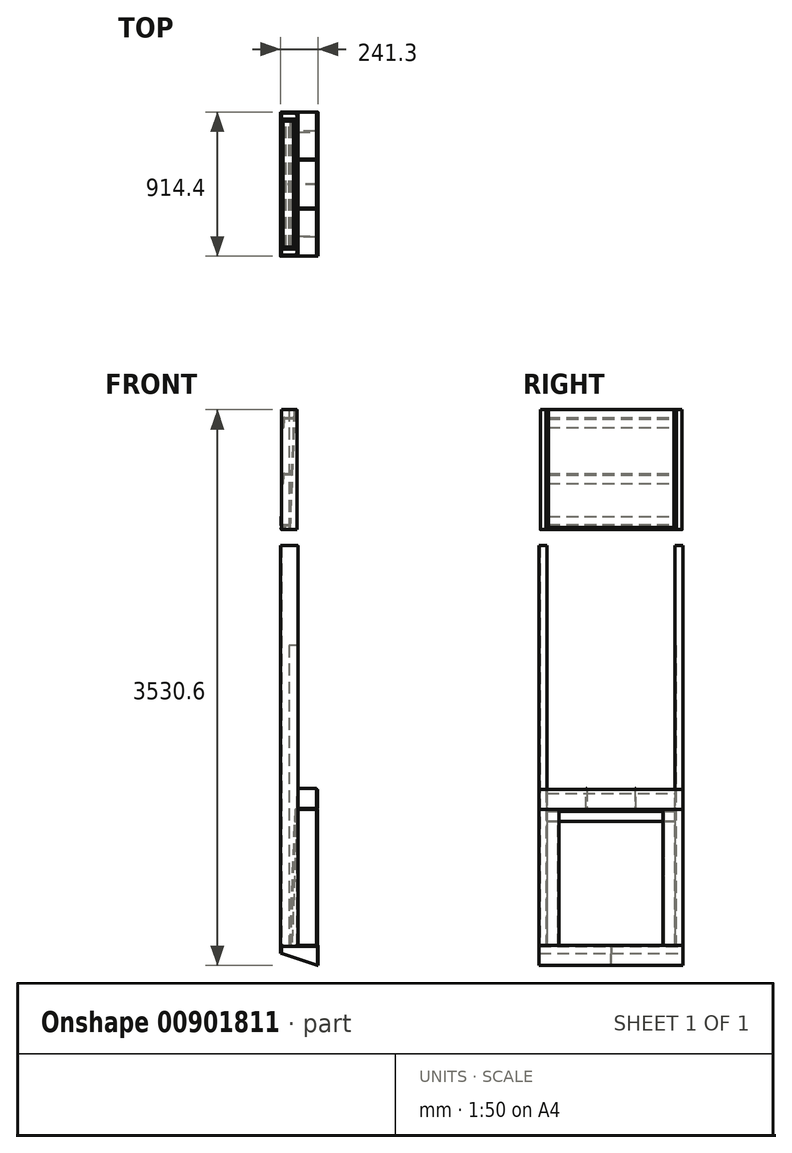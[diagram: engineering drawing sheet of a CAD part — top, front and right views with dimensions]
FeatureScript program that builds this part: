
annotation { "Feature Type Name" : "Feature", "Feature Type Description" : "" }
export const myFeature = defineFeature(function(context is Context, id is Id, definition is map)
    precondition{}
    {
        {
            var Q0;
            Q0=qCreatedBy(makeId("Front.planeOp"),FACE);
            var sketch = newSketch(context, id + "F0", { "sketchPlane" : qUnion([Q0])});
            skLineSegment(sketch, "E0", {"start": v(6.35, -50.8) * mm, "end": v(6.35, -19.05) * mm});
            skLineSegment(sketch, "E1", {"start": v(19.05, -6.35) * mm, "end": v(95.25, -6.35) * mm});
            skLineSegment(sketch, "E2", {"start": v(107.95, -19.05) * mm, "end": v(107.95, -127) * mm});
            skLineSegment(sketch, "E3", {"start": v(107.95, -127) * mm, "end": v(114.3, -127) * mm});
            skLineSegment(sketch, "E4", {"start": v(114.3, -127) * mm, "end": v(114.3, -12.7) * mm});
            skLineSegment(sketch, "E5", {"start": v(101.6, 0) * mm, "end": v(12.7, 0) * mm});
            skLineSegment(sketch, "E6", {"start": v(0, -12.7) * mm, "end": v(0, -50.8) * mm});
            skLineSegment(sketch, "E7", {"start": v(0, -50.8) * mm, "end": v(6.35, -50.8) * mm});
            skPoint(sketch, "E8.visualSharp", {"position": v(107.95, -6.35) * mm});
            skArc(sketch, "E8.filletArc", {"start": v(107.95, -19.05) * mm, "mid": v(104.23, -10.07) * mm, "end": v(95.25, -6.35) * mm});
            skPoint(sketch, "E9.visualSharp", {"position": v(6.35, -6.35) * mm});
            skArc(sketch, "E9.filletArc", {"start": v(19.05, -6.35) * mm, "mid": v(10.07, -10.07) * mm, "end": v(6.35, -19.05) * mm});
            skPoint(sketch, "E10.visualSharp", {"position": v(114.3, 0) * mm});
            skArc(sketch, "E10.filletArc", {"start": v(114.3, -12.7) * mm, "mid": v(110.58, -3.72) * mm, "end": v(101.6, 0) * mm});
            skPoint(sketch, "E11.visualSharp", {"position": v(0, 0) * mm});
            skArc(sketch, "E11.filletArc", {"start": v(12.7, 0) * mm, "mid": v(3.72, -3.72) * mm, "end": v(0, -12.7) * mm});
            skLineSegment(sketch, "E12", {"start": v(95.25, -6.35) * mm, "end": v(95.25, 0) * mm});
            skLineSegment(sketch, "E13", {"start": v(95.25, -6.35) * mm, "end": v(95.25, -127) * mm});
            skLineSegment(sketch, "E14", {"start": v(95.25, -127) * mm, "end": v(107.95, -127) * mm});
            skLineSegment(sketch, "E15", {"start": v(95.25, -6.35) * mm, "end": v(228.6, -6.35) * mm});
            skLineSegment(sketch, "E16", {"start": v(234.95, -12.7) * mm, "end": v(234.95, -127) * mm});
            skLineSegment(sketch, "E17", {"start": v(234.95, -127) * mm, "end": v(241.3, -127) * mm});
            skLineSegment(sketch, "E18", {"start": v(241.3, -127) * mm, "end": v(241.3, -6.35) * mm});
            skLineSegment(sketch, "E19", {"start": v(234.95, 0) * mm, "end": v(101.6, 0) * mm});
            skLineSegment(sketch, "E20", {"start": v(114.3, -12.7) * mm, "end": v(114.3, -6.35) * mm});
            skPoint(sketch, "E21.visualSharp", {"position": v(234.95, -6.35) * mm});
            skArc(sketch, "E21.filletArc", {"start": v(234.95, -12.7) * mm, "mid": v(233.1, -8.2) * mm, "end": v(228.6, -6.35) * mm});
            skPoint(sketch, "E22.visualSharp", {"position": v(241.3, 0) * mm});
            skArc(sketch, "E22.filletArc", {"start": v(241.3, -6.35) * mm, "mid": v(239.44, -1.86) * mm, "end": v(234.95, 0) * mm});
            skSolve(sketch);
        }
        {
            var Q0;
            Q0=makeQuery(id+"F0.imprint","IMPRINT",FACE,{"disambiguationData":[TD([[makeQuery(id+"F0.imprint","IMPRINT",EDGE,{"derivedFrom":sQuery(id+"F0.wireOp",EDGE,"E0")}),1.0]])]});
            var Q1;
            {var subQ3=sQuery(id+"F0.wireOp",EDGE,"E12");Q1=makeQuery(id+"F0.imprint","IMPRINT",FACE,{"disambiguationData":[TD([[makeQuery(id+"F0.imprint","IMPRINT",EDGE,{"derivedFrom":subQ3}),-1.0]])]});}
            extrude(context, id + "F1", {"entities" : qUnion([Q0, Q1]), "endBound" : BoundingType.SYMMETRIC, "depth" : 914.4 * mm, "offsetDistance" : 25.4 * mm});
        }
        {
            var Q0;
            Q0=makeQuery(id+"F1.opExtrude","SWEPT_FACE",FACE,{"disambiguationData":[OSD([sQuery(id+"F0.wireOp",EDGE,"E5")])]});
            var sketch = newSketch(context, id + "F2", { "sketchPlane" : qUnion([Q0])});
            skLineSegment(sketch, "E23", {"start": v(112.6, 406.4) * mm, "end": v(112.6, 444.5) * mm});
            skLineSegment(sketch, "E24", {"start": v(99.9, 457.2) * mm, "end": v(12.7, 457.2) * mm});
            skLineSegment(sketch, "E25", {"start": v(0, 444.5) * mm, "end": v(0, 406.4) * mm});
            skLineSegment(sketch, "E26", {"start": v(0, 406.4) * mm, "end": v(6.35, 406.4) * mm});
            skLineSegment(sketch, "E27", {"start": v(6.35, 406.4) * mm, "end": v(6.35, 438.15) * mm});
            skLineSegment(sketch, "E28", {"start": v(19.05, 450.85) * mm, "end": v(93.55, 450.85) * mm});
            skLineSegment(sketch, "E29", {"start": v(106.25, 438.15) * mm, "end": v(106.25, 406.4) * mm});
            skLineSegment(sketch, "E30", {"start": v(106.25, 406.4) * mm, "end": v(112.6, 406.4) * mm});
            skPoint(sketch, "E31.visualSharp", {"position": v(106.25, 450.85) * mm});
            skArc(sketch, "E31.filletArc", {"start": v(106.25, 438.15) * mm, "mid": v(102.53, 447.13) * mm, "end": v(93.55, 450.85) * mm});
            skPoint(sketch, "E32.visualSharp", {"position": v(112.6, 457.2) * mm});
            skArc(sketch, "E32.filletArc", {"start": v(112.6, 444.5) * mm, "mid": v(108.88, 453.48) * mm, "end": v(99.9, 457.2) * mm});
            skPoint(sketch, "E33.visualSharp", {"position": v(6.35, 450.85) * mm});
            skArc(sketch, "E33.filletArc", {"start": v(19.05, 450.85) * mm, "mid": v(10.07, 447.13) * mm, "end": v(6.35, 438.15) * mm});
            skPoint(sketch, "E34.visualSharp", {"position": v(0, 457.2) * mm});
            skArc(sketch, "E34.filletArc", {"start": v(12.7, 457.2) * mm, "mid": v(3.72, 453.48) * mm, "end": v(0, 444.5) * mm});
            skLineSegment(sketch, "E35", {"start": v(106.25, 406.4) * mm, "end": v(55.45, 406.4) * mm});
            skLineSegment(sketch, "E36", {"start": v(55.45, 406.4) * mm, "end": v(55.45, 412.75) * mm});
            skLineSegment(sketch, "E37", {"start": v(55.45, 412.75) * mm, "end": v(106.25, 412.75) * mm});
            skSolve(sketch);
        }
        {
            var Q0;
            Q0=makeQuery(id+"F2.imprint","IMPRINT",FACE,{"disambiguationData":[TD([[makeQuery(id+"F2.imprint","IMPRINT",EDGE,{"derivedFrom":sQuery(id+"F2.wireOp",EDGE,"E23")}),1.0]])]});
            var Q1;
            {var subQ5=sQuery(id+"F2.wireOp",EDGE,"E24");Q1=makeQuery(id+"F2.imprint","IMPRINT",FACE,{"disambiguationData":[TD([[makeQuery(id+"F2.imprint","IMPRINT",EDGE,{"derivedFrom":subQ5}),1.0]])]});}
            var Q2;
            Q2=makeQuery(id+"F2.imprint","IMPRINT",FACE,{"disambiguationData":[TD([[makeQuery(id+"F2.imprint","IMPRINT",EDGE,{"derivedFrom":sQuery(id+"F2.wireOp",EDGE,"E25")}),1.0]])]});
            extrude(context, id + "F3", {"entities" : qUnion([Q0, Q1, Q2]), "depth" : 2540 * mm, "offsetDistance" : 25.4 * mm});
        }
        {
            var Q0;
            Q0=makeQuery(id+"F3.opExtrude","SWEPT_BODY",BODY,{"disambiguationData":[OSD([sQuery(id+"F2.wireOp",EDGE,"E23"),sQuery(id+"F2.wireOp",EDGE,"E24"),sQuery(id+"F2.wireOp",EDGE,"E25"),sQuery(id+"F2.wireOp",EDGE,"E26"),sQuery(id+"F2.wireOp",EDGE,"E27"),sQuery(id+"F2.wireOp",EDGE,"E28"),sQuery(id+"F2.wireOp",EDGE,"E29"),sQuery(id+"F2.wireOp",EDGE,"E30"),sQuery(id+"F2.wireOp",EDGE,"E31.filletArc"),sQuery(id+"F2.wireOp",EDGE,"E32.filletArc"),sQuery(id+"F2.wireOp",EDGE,"E33.filletArc"),sQuery(id+"F2.wireOp",EDGE,"E34.filletArc")])]});
            var Q1;
            Q1=qCreatedBy(makeId("Front.planeOp"),FACE);
            mirror(context, id + "F4", {"operationType" : NewBodyOperationType.ADD, "entities" : qUnion([Q0]), "mirrorPlane" : qUnion([Q1])});
        }
        {
            var Q0;
            {var subQ1=sQuery(id+"F2.wireOp",EDGE,"E29");var subQ3=sQuery(id+"F2.wireOp",EDGE,"E37");var subQ4=makeQuery(id+"F2.imprint","INTERSECT",VERTEX,{"derivedFrom":[subQ1,subQ3]});Q0=makeQuery(id+"F2.imprint","IMPRINT",FACE,{"disambiguationData":[TD([[makeQuery(id+"F2.imprint","IMPRINT",EDGE,{"disambiguationData":[TD([[subQ4,-1.0]])],"derivedFrom":subQ1}),-1.0]])]});}
            var Q1;
            {var subQ0=sQuery(id+"F2.wireOp",EDGE,"E36");Q1=makeQuery(id+"F2.imprint","IMPRINT",FACE,{"disambiguationData":[TD([[makeQuery(id+"F2.imprint","IMPRINT",EDGE,{"derivedFrom":subQ0}),-1.0]])]});}
            extrude(context, id + "F5", {"entities" : qUnion([Q0, Q1]), "depth" : 1905 * mm, "offsetDistance" : 25.4 * mm});
        }
        {
            var Q0;
            Q0=makeQuery(id+"F5.opExtrude","SWEPT_BODY",BODY,{"disambiguationData":[OSD([sQuery(id+"F2.wireOp",EDGE,"E29"),sQuery(id+"F2.wireOp",EDGE,"E35"),sQuery(id+"F2.wireOp",EDGE,"E36"),sQuery(id+"F2.wireOp",EDGE,"E37")])]});
            var Q1;
            Q1=qCreatedBy(makeId("Front.planeOp"),FACE);
            mirror(context, id + "F6", {"entities" : qUnion([Q0]), "mirrorPlane" : qUnion([Q1])});
        }
        {
            var Q0;
            Q0=makeQuery(id+"F5.opExtrude","SWEPT_FACE",FACE,{"disambiguationData":[OSD([sQuery(id+"F2.wireOp",EDGE,"E35")])]});
            var sketch = newSketch(context, id + "F7", { "sketchPlane" : qUnion([Q0])});
            skLineSegment(sketch, "E38", {"start": v(68.15, 0) * mm, "end": v(99.9, 863.83) * mm});
            skLineSegment(sketch, "E39", {"start": v(99.9, 863.83) * mm, "end": v(106.25, 863.6) * mm});
            skLineSegment(sketch, "E40", {"start": v(106.25, 863.6) * mm, "end": v(74.5, 0) * mm});
            skLineSegment(sketch, "E41", {"start": v(74.5, 0) * mm, "end": v(68.15, 0) * mm});
            skLineSegment(sketch, "E42", {"start": v(106.25, 863.6) * mm, "end": v(112.6, 863.6) * mm});
            skLineSegment(sketch, "E43", {"start": v(112.6, 863.6) * mm, "end": v(112.6, 965.2) * mm});
            skLineSegment(sketch, "E44", {"start": v(112.6, 965.2) * mm, "end": v(106.25, 965.2) * mm});
            skLineSegment(sketch, "E45", {"start": v(106.25, 965.2) * mm, "end": v(106.25, 863.6) * mm});
            skLineSegment(sketch, "E46", {"start": v(106.25, 870.18) * mm, "end": v(99.9, 863.83) * mm});
            skLineSegment(sketch, "E47", {"start": v(112.6, 863.6) * mm, "end": v(105.82, 851.85) * mm});
            skLineSegment(sketch, "E48", {"start": v(103.45, 787.45) * mm, "end": v(97.1, 787.68) * mm});
            skSolve(sketch);
        }
        {
            var Q0;
            {var subQ4=sQuery(id+"F7.wireOp",EDGE,"E42");Q0=makeQuery(id+"F7.imprint","IMPRINT",FACE,{"disambiguationData":[TD([[makeQuery(id+"F7.imprint","IMPRINT",EDGE,{"derivedFrom":subQ4}),1.0]])]});}
            var Q1;
            {var subQ0=sQuery(id+"F7.wireOp",EDGE,"E39");Q1=makeQuery(id+"F7.imprint","IMPRINT",FACE,{"disambiguationData":[TD([[makeQuery(id+"F7.imprint","IMPRINT",EDGE,{"derivedFrom":subQ0}),1.0]])]});}
            var Q2;
            {var subQ0=sQuery(id+"F7.wireOp",EDGE,"E42");Q2=makeQuery(id+"F7.imprint","IMPRINT",FACE,{"disambiguationData":[TD([[makeQuery(id+"F7.imprint","IMPRINT",EDGE,{"derivedFrom":subQ0}),-1.0]])]});}
            var Q3;
            Q3=makeQuery(id+"F6.opPattern","COPY",FACE,{"derivedFrom":makeQuery(id+"F5.opExtrude","SWEPT_FACE",FACE,{"disambiguationData":[OSD([sQuery(id+"F2.wireOp",EDGE,"E35")])]}),"instanceName":"1"});
            extrude(context, id + "F8", {"entities" : qUnion([Q0, Q1, Q2]), "endBound" : BoundingType.UP_TO_SURFACE, "depth" : 25.4 * mm, "endBoundEntityFace" : qUnion([Q3]), "offsetDistance" : 25.4 * mm});
        }
        {
            var Q0;
            {var subQ3=sQuery(id+"F7.wireOp",EDGE,"E39");Q0=makeQuery(id+"F7.imprint","IMPRINT",FACE,{"disambiguationData":[TD([[makeQuery(id+"F7.imprint","IMPRINT",EDGE,{"derivedFrom":subQ3}),-1.0]])]});}
            var Q1;
            Q1=makeQuery(id+"F6.opPattern","COPY",FACE,{"derivedFrom":makeQuery(id+"F5.opExtrude","SWEPT_FACE",FACE,{"disambiguationData":[OSD([sQuery(id+"F2.wireOp",EDGE,"E35")])]}),"instanceName":"1"});
            extrude(context, id + "F9", {"entities" : qUnion([Q0]), "endBound" : BoundingType.UP_TO_SURFACE, "depth" : 25.4 * mm, "endBoundEntityFace" : qUnion([Q1]), "offsetDistance" : 25.4 * mm});
        }
        {
            var Q0;
            {var subQ0=sQuery(id+"F7.wireOp",EDGE,"E41");Q0=makeQuery(id+"F7.imprint","IMPRINT",FACE,{"disambiguationData":[TD([[makeQuery(id+"F7.imprint","IMPRINT",EDGE,{"derivedFrom":subQ0}),-1.0]])]});}
            extrude(context, id + "F10", {"entities" : qUnion([Q0]), "depth" : 76.2 * mm, "offsetDistance" : 25.4 * mm});
        }
        {
            var Q0;
            Q0=makeQuery(id+"F10.opExtrude","SWEPT_BODY",BODY,{"disambiguationData":[OSD([sQuery(id+"F7.wireOp",EDGE,"E38"),sQuery(id+"F7.wireOp",EDGE,"E40"),sQuery(id+"F7.wireOp",EDGE,"E41"),sQuery(id+"F7.wireOp",EDGE,"E48")])]});
            var Q1;
            Q1=qCreatedBy(makeId("Front.planeOp"),FACE);
            mirror(context, id + "F11", {"entities" : qUnion([Q0]), "mirrorPlane" : qUnion([Q1])});
        }
        {
            var Q0;
            Q0=makeQuery(id+"F1.opExtrude","SWEPT_FACE",FACE,{"disambiguationData":[OSD([sQuery(id+"F0.wireOp",EDGE,"E5")])]});
            var sketch = newSketch(context, id + "F12", { "sketchPlane" : qUnion([Q0])});
            skLineSegment(sketch, "E49", {"start": v(61.8, 406.4) * mm, "end": v(61.8, 330.2) * mm});
            skLineSegment(sketch, "E50", {"start": v(68.15, 330.2) * mm, "end": v(68.15, 406.4) * mm});
            skLineSegment(sketch, "E51", {"start": v(68.15, 406.4) * mm, "end": v(61.8, 406.4) * mm});
            skLineSegment(sketch, "E52", {"start": v(61.8, 330.2) * mm, "end": v(68.15, 330.2) * mm});
            skSolve(sketch);
        }
        {
            var Q0;
            Q0=makeQuery(id+"F12.imprint","IMPRINT",FACE,{"disambiguationData":[TD([[makeQuery(id+"F12.imprint","IMPRINT",EDGE,{"derivedFrom":sQuery(id+"F12.wireOp",EDGE,"E49")}),1.0]])]});
            var Q1;
            Q1=makeQuery(id+"F10.opExtrude","CAP_EDGE",EDGE,{"disambiguationData":[OSD([sQuery(id+"F7.wireOp",EDGE,"E38")])],"isStart":false});
            sweep(context, id + "F13", {"profiles" : qUnion([Q0]), "path" : qUnion([Q1])});
        }
        {
            var Q0;
            Q0=makeQuery(id+"F13.opSweep","SWEPT_BODY",BODY,{"disambiguationData":[OSD([sQuery(id+"F7.wireOp",EDGE,"E38"),sQuery(id+"F12.wireOp",EDGE,"E49"),sQuery(id+"F12.wireOp",EDGE,"E50"),sQuery(id+"F12.wireOp",EDGE,"E51"),sQuery(id+"F12.wireOp",EDGE,"E52")])]});
            var Q1;
            Q1=qCreatedBy(makeId("Front.planeOp"),FACE);
            mirror(context, id + "F14", {"entities" : qUnion([Q0]), "mirrorPlane" : qUnion([Q1])});
        }
        {
            var Q0;
            Q0=makeQuery(id+"F5.opExtrude","SWEPT_FACE",FACE,{"disambiguationData":[OSD([sQuery(id+"F2.wireOp",EDGE,"E35")])]});
            var sketch = newSketch(context, id + "F15", { "sketchPlane" : qUnion([Q0])});
            skLineSegment(sketch, "E53", {"start": v(90.75, 787.68) * mm, "end": v(93.56, 864.07) * mm});
            skLineSegment(sketch, "E54", {"start": v(97.1, 787.68) * mm, "end": v(99.9, 863.83) * mm});
            skLineSegment(sketch, "E55", {"start": v(93.56, 864.07) * mm, "end": v(99.9, 863.83) * mm});
            skLineSegment(sketch, "E56", {"start": v(97.1, 787.68) * mm, "end": v(90.75, 787.68) * mm});
            skSolve(sketch);
        }
        {
            var Q0;
            Q0=makeQuery(id+"F15.imprint","IMPRINT",FACE,{"disambiguationData":[TD([[makeQuery(id+"F15.imprint","IMPRINT",EDGE,{"derivedFrom":sQuery(id+"F15.wireOp",EDGE,"E53")}),-1.0]])]});
            var Q1;
            Q1=makeQuery(id+"F6.opPattern","COPY",FACE,{"derivedFrom":makeQuery(id+"F5.opExtrude","SWEPT_FACE",FACE,{"disambiguationData":[OSD([sQuery(id+"F2.wireOp",EDGE,"E35")])]}),"instanceName":"1"});
            extrude(context, id + "F16", {"entities" : qUnion([Q0]), "endBound" : BoundingType.UP_TO_SURFACE, "depth" : 25.4 * mm, "endBoundEntityFace" : qUnion([Q1]), "offsetDistance" : 25.4 * mm});
        }
        {
            var Q0;
            Q0=makeQuery(id+"F3.opExtrude","CAP_FACE",FACE,{"disambiguationData":[OSD([sQuery(id+"F2.wireOp",EDGE,"E23"),sQuery(id+"F2.wireOp",EDGE,"E24"),sQuery(id+"F2.wireOp",EDGE,"E25"),sQuery(id+"F2.wireOp",EDGE,"E26"),sQuery(id+"F2.wireOp",EDGE,"E27"),sQuery(id+"F2.wireOp",EDGE,"E28"),sQuery(id+"F2.wireOp",EDGE,"E29"),sQuery(id+"F2.wireOp",EDGE,"E30"),sQuery(id+"F2.wireOp",EDGE,"E31.filletArc"),sQuery(id+"F2.wireOp",EDGE,"E32.filletArc"),sQuery(id+"F2.wireOp",EDGE,"E33.filletArc"),sQuery(id+"F2.wireOp",EDGE,"E34.filletArc")])],"isStart":false});
            cPlane(context, id + "F17", {"entities" : qUnion([Q0]), "cplaneType" : CPlaneType.OFFSET, "offset" : 101.6 * mm, "width" : 152.4 * mm, "height" : 152.4 * mm});
        }
        {
            var Q0;
            Q0=qCreatedBy(id+"F17.planeOp",FACE);
            var sketch = newSketch(context, id + "F18", { "sketchPlane" : qUnion([Q0])});
            skLineSegment(sketch, "E57", {"start": v(104.98, 414.02) * mm, "end": v(7.62, 414.02) * mm});
            skLineSegment(sketch, "E58", {"start": v(7.62, 414.02) * mm, "end": v(7.62, 436.88) * mm});
            skLineSegment(sketch, "E59", {"start": v(20.32, 449.58) * mm, "end": v(92.28, 449.58) * mm});
            skLineSegment(sketch, "E60", {"start": v(104.98, 436.88) * mm, "end": v(104.98, 414.02) * mm});
            skPoint(sketch, "E61.visualSharp", {"position": v(104.98, 449.58) * mm});
            skArc(sketch, "E61.filletArc", {"start": v(104.98, 436.88) * mm, "mid": v(101.26, 445.86) * mm, "end": v(92.28, 449.58) * mm});
            skPoint(sketch, "E62.visualSharp", {"position": v(7.62, 449.58) * mm});
            skArc(sketch, "E62.filletArc", {"start": v(20.32, 449.58) * mm, "mid": v(11.34, 445.86) * mm, "end": v(7.62, 436.88) * mm});
            skLineSegment(sketch, "E63", {"start": v(54.18, 414.02) * mm, "end": v(54.18, 405.13) * mm});
            skLineSegment(sketch, "E64", {"start": v(54.18, 405.13) * mm, "end": v(7.62, 405.13) * mm});
            skLineSegment(sketch, "E65", {"start": v(7.62, 405.13) * mm, "end": v(7.62, 414.02) * mm});
            skLineSegment(sketch, "E66", {"start": v(54.18, 405.13) * mm, "end": v(61.8, 405.13) * mm});
            skLineSegment(sketch, "E67", {"start": v(61.8, 405.13) * mm, "end": v(61.8, 398.78) * mm});
            skLineSegment(sketch, "E68", {"start": v(61.8, 398.78) * mm, "end": v(7.62, 398.78) * mm});
            skLineSegment(sketch, "E69", {"start": v(7.62, 398.78) * mm, "end": v(7.62, 405.13) * mm});
            skSolve(sketch);
        }
        {
            var Q0;
            Q0=makeQuery(id+"F18.imprint","IMPRINT",FACE,{"disambiguationData":[TD([[makeQuery(id+"F18.imprint","IMPRINT",EDGE,{"derivedFrom":sQuery(id+"F18.wireOp",EDGE,"E57")}),-1.0]])]});
            extrude(context, id + "F19", {"entities" : qUnion([Q0]), "depth" : 762 * mm, "offsetDistance" : 25.4 * mm});
        }
        {
            var Q0;
            Q0=makeQuery(id+"F19.opExtrude","SWEPT_BODY",BODY,{"disambiguationData":[OSD([sQuery(id+"F18.wireOp",EDGE,"E57"),sQuery(id+"F18.wireOp",EDGE,"E58"),sQuery(id+"F18.wireOp",EDGE,"E59"),sQuery(id+"F18.wireOp",EDGE,"E60"),sQuery(id+"F18.wireOp",EDGE,"E61.filletArc"),sQuery(id+"F18.wireOp",EDGE,"E62.filletArc")])]});
            var Q1;
            Q1=qCreatedBy(makeId("Front.planeOp"),FACE);
            mirror(context, id + "F20", {"entities" : qUnion([Q0]), "mirrorPlane" : qUnion([Q1])});
        }
        {
            var Q0;
            {var subQ2=sQuery(id+"F18.wireOp",EDGE,"E63");Q0=makeQuery(id+"F18.imprint","IMPRINT",FACE,{"disambiguationData":[TD([[makeQuery(id+"F18.imprint","IMPRINT",EDGE,{"derivedFrom":subQ2}),-1.0]])]});}
            extrude(context, id + "F21", {"entities" : qUnion([Q0]), "depth" : 762 * mm, "offsetDistance" : 25.4 * mm});
        }
        {
            var Q0;
            Q0=makeQuery(id+"F21.opExtrude","CAP_FACE",FACE,{"disambiguationData":[OSD([sQuery(id+"F18.wireOp",EDGE,"E57"),sQuery(id+"F18.wireOp",EDGE,"E63"),sQuery(id+"F18.wireOp",EDGE,"E64"),sQuery(id+"F18.wireOp",EDGE,"E65")])],"isStart":false});
            var sketch = newSketch(context, id + "F22", { "sketchPlane" : qUnion([Q0])});
            skLineSegment(sketch, "E70", {"start": v(7.62, 405.13) * mm, "end": v(7.62, 398.78) * mm});
            skLineSegment(sketch, "E71", {"start": v(7.62, 398.78) * mm, "end": v(93.56, 398.78) * mm});
            skLineSegment(sketch, "E72", {"start": v(93.56, 398.78) * mm, "end": v(93.56, 405.13) * mm});
            skLineSegment(sketch, "E73", {"start": v(93.56, 405.13) * mm, "end": v(7.62, 405.13) * mm});
            skSolve(sketch);
        }
        {
            var Q1;
            {var subQ3=sQuery(id+"F22.wireOp",EDGE,"E70");Q1=makeQuery(id+"F22.imprint","IMPRINT",FACE,{"disambiguationData":[TD([[makeQuery(id+"F22.imprint","IMPRINT",EDGE,{"derivedFrom":subQ3}),1.0]])]});}
            var Q2;
            Q2=makeQuery(id+"F18.imprint","IMPRINT",FACE,{"disambiguationData":[TD([[makeQuery(id+"F18.imprint","IMPRINT",EDGE,{"derivedFrom":sQuery(id+"F18.wireOp",EDGE,"E64")}),1.0]])]});
            loft(context, id + "F23", {"sheetProfilesArray" : [{ "sheetProfileEntities" : qUnion([Q1]) }, { "sheetProfileEntities" : qUnion([Q2]) }]});
        }
        {
            var Q0;
            {var subQ3=sQuery(id+"F22.wireOp",EDGE,"E70");Q0=makeQuery(id+"F23.opLoft","SWEPT_BODY",BODY,{"disambiguationData":[OSD([makeQuery(id+"F18.imprint","IMPRINT",FACE,{"disambiguationData":[TD([[makeQuery(id+"F18.imprint","IMPRINT",EDGE,{"derivedFrom":sQuery(id+"F18.wireOp",EDGE,"E64")}),1.0]])]}),makeQuery(id+"F22.imprint","IMPRINT",FACE,{"disambiguationData":[TD([[makeQuery(id+"F22.imprint","IMPRINT",EDGE,{"derivedFrom":subQ3}),1.0]])]})])]});}
            var Q1;
            Q1=makeQuery(id+"F21.opExtrude","SWEPT_BODY",BODY,{"disambiguationData":[OSD([sQuery(id+"F18.wireOp",EDGE,"E57"),sQuery(id+"F18.wireOp",EDGE,"E63"),sQuery(id+"F18.wireOp",EDGE,"E64"),sQuery(id+"F18.wireOp",EDGE,"E65")])]});
            var Q2;
            Q2=qCreatedBy(makeId("Front.planeOp"),FACE);
            mirror(context, id + "F24", {"entities" : qUnion([Q0, Q1]), "mirrorPlane" : qUnion([Q2])});
        }
        {
            var Q0;
            Q0=makeQuery(id+"F23.opLoft","SWEPT_FACE",FACE,{"disambiguationData":[OSD([sQuery(id+"F18.wireOp",EDGE,"E67"),sQuery(id+"F18.wireOp",EDGE,"E68"),sQuery(id+"F18.wireOp",EDGE,"E69"),sQuery(id+"F22.wireOp",EDGE,"E70"),sQuery(id+"F22.wireOp",EDGE,"E71"),sQuery(id+"F22.wireOp",EDGE,"E72")])]});
            var sketch = newSketch(context, id + "F25", { "sketchPlane" : qUnion([Q0])});
            skLineSegment(sketch, "E74", {"start": v(93.56, 3403.6) * mm, "end": v(87.22, 3403.86) * mm});
            skLineSegment(sketch, "E75", {"start": v(87.22, 3403.86) * mm, "end": v(55.98, 2654.55) * mm});
            skLineSegment(sketch, "E76", {"start": v(55.98, 2654.55) * mm, "end": v(62.33, 2654.29) * mm});
            skLineSegment(sketch, "E77", {"start": v(62.33, 2654.29) * mm, "end": v(93.56, 3403.6) * mm});
            skLineSegment(sketch, "E78", {"start": v(5.97, 2667) * mm, "end": v(5.97, 2673.35) * mm});
            skLineSegment(sketch, "E79", {"start": v(5.97, 2673.35) * mm, "end": v(56.77, 2673.35) * mm});
            skLineSegment(sketch, "E80", {"start": v(5.97, 2667) * mm, "end": v(56.5, 2667) * mm});
            skLineSegment(sketch, "E81", {"start": v(56.5, 2667) * mm, "end": v(56.77, 2673.35) * mm});
            skLineSegment(sketch, "E82", {"start": v(36.38, 2641.6) * mm, "end": v(36.38, 2650.5) * mm});
            skLineSegment(sketch, "E83", {"start": v(36.38, 2650.5) * mm, "end": v(5.97, 2650.5) * mm});
            skLineSegment(sketch, "E84", {"start": v(5.97, 2650.5) * mm, "end": v(5.97, 2667) * mm});
            skLineSegment(sketch, "E85", {"start": v(5.97, 2650.5) * mm, "end": v(5.97, 2641.6) * mm});
            skLineSegment(sketch, "E86", {"start": v(5.97, 2641.6) * mm, "end": v(36.38, 2641.6) * mm});
            skLineSegment(sketch, "E87", {"start": v(5.97, 2644.14) * mm, "end": v(36.38, 2644.14) * mm});
            skLineSegment(sketch, "E88", {"start": v(5.97, 2673.35) * mm, "end": v(5.97, 2724.15) * mm});
            skLineSegment(sketch, "E89", {"start": v(5.97, 2724.15) * mm, "end": v(12.32, 2724.15) * mm});
            skLineSegment(sketch, "E90", {"start": v(12.32, 2724.15) * mm, "end": v(12.32, 2673.35) * mm});
            skSolve(sketch);
        }
        {
            var Q0;
            {var subQ0=sQuery(id+"F25.wireOp",EDGE,"E76");Q0=makeQuery(id+"F25.imprint","IMPRINT",FACE,{"disambiguationData":[TD([[makeQuery(id+"F25.imprint","IMPRINT",EDGE,{"derivedFrom":subQ0}),1.0]])]});}
            var Q1;
            Q1=makeQuery(id+"F24.opPattern","COPY",FACE,{"derivedFrom":makeQuery(id+"F23.opLoft","SWEPT_FACE",FACE,{"disambiguationData":[OSD([sQuery(id+"F18.wireOp",EDGE,"E67"),sQuery(id+"F18.wireOp",EDGE,"E68"),sQuery(id+"F18.wireOp",EDGE,"E69"),sQuery(id+"F22.wireOp",EDGE,"E70"),sQuery(id+"F22.wireOp",EDGE,"E71"),sQuery(id+"F22.wireOp",EDGE,"E72")])]}),"instanceName":"1"});
            extrude(context, id + "F26", {"entities" : qUnion([Q0]), "endBound" : BoundingType.UP_TO_SURFACE, "depth" : 25.4 * mm, "endBoundEntityFace" : qUnion([Q1]), "offsetDistance" : 25.4 * mm});
        }
        {
            var Q0;
            {var subQ0=sQuery(id+"F25.wireOp",EDGE,"E87");var subQ1=sQuery(id+"F25.wireOp",EDGE,"E82");var subQ2=makeQuery(id+"F25.imprint","INTERSECT",VERTEX,{"derivedFrom":[subQ1,subQ0]});var subQ9=sQuery(id+"F25.wireOp",EDGE,"E85");var subQ11=makeQuery(id+"F25.imprint","INTERSECT",VERTEX,{"derivedFrom":[subQ9,subQ0]});Q0=qUnion([makeQuery(id+"F25.imprint","IMPRINT",FACE,{"disambiguationData":[TD([[makeQuery(id+"F25.imprint","IMPRINT",EDGE,{"disambiguationData":[TD([[subQ11,1.0]])],"derivedFrom":subQ9}),1.0]])]}),makeQuery(id+"F25.imprint","IMPRINT",FACE,{"disambiguationData":[TD([[makeQuery(id+"F25.imprint","IMPRINT",EDGE,{"disambiguationData":[TD([[subQ2,-1.0]])],"derivedFrom":subQ1}),1.0]])]})]);}
            var Q1;
            Q1=makeQuery(id+"F24.opPattern","COPY",FACE,{"derivedFrom":makeQuery(id+"F23.opLoft","SWEPT_FACE",FACE,{"disambiguationData":[OSD([sQuery(id+"F18.wireOp",EDGE,"E67"),sQuery(id+"F18.wireOp",EDGE,"E68"),sQuery(id+"F18.wireOp",EDGE,"E69"),sQuery(id+"F22.wireOp",EDGE,"E70"),sQuery(id+"F22.wireOp",EDGE,"E71"),sQuery(id+"F22.wireOp",EDGE,"E72")])]}),"instanceName":"1"});
            extrude(context, id + "F27", {"entities" : qUnion([Q0]), "endBound" : BoundingType.UP_TO_SURFACE, "depth" : 25.4 * mm, "endBoundEntityFace" : qUnion([Q1]), "offsetDistance" : 25.4 * mm});
        }
        {
            var Q0;
            {var subQ8=sQuery(id+"F25.wireOp",EDGE,"E76");Q0=makeQuery(id+"F25.imprint","IMPRINT",FACE,{"disambiguationData":[TD([[makeQuery(id+"F25.imprint","IMPRINT",EDGE,{"derivedFrom":subQ8}),-1.0]])]});}
            var Q1;
            Q1=makeQuery(id+"F24.opPattern","COPY",FACE,{"derivedFrom":makeQuery(id+"F23.opLoft","SWEPT_FACE",FACE,{"disambiguationData":[OSD([sQuery(id+"F18.wireOp",EDGE,"E67"),sQuery(id+"F18.wireOp",EDGE,"E68"),sQuery(id+"F18.wireOp",EDGE,"E69"),sQuery(id+"F22.wireOp",EDGE,"E70"),sQuery(id+"F22.wireOp",EDGE,"E71"),sQuery(id+"F22.wireOp",EDGE,"E72")])]}),"instanceName":"1"});
            extrude(context, id + "F28", {"entities" : qUnion([Q0]), "endBound" : BoundingType.UP_TO_SURFACE, "depth" : 25.4 * mm, "endBoundEntityFace" : qUnion([Q1]), "offsetDistance" : 25.4 * mm});
        }
        {
            var Q0;
            {var subQ0=sQuery(id+"F25.wireOp",EDGE,"E78");Q0=makeQuery(id+"F25.imprint","IMPRINT",FACE,{"disambiguationData":[TD([[makeQuery(id+"F25.imprint","IMPRINT",EDGE,{"derivedFrom":subQ0}),-1.0]])]});}
            var Q1;
            {var subQ0=sQuery(id+"F25.wireOp",EDGE,"E80");var subQ1=sQuery(id+"F25.wireOp",EDGE,"E75");var subQ2=makeQuery(id+"F25.imprint","INTERSECT",VERTEX,{"derivedFrom":[subQ1,subQ0]});Q1=makeQuery(id+"F25.imprint","IMPRINT",FACE,{"disambiguationData":[TD([[makeQuery(id+"F25.imprint","IMPRINT",EDGE,{"disambiguationData":[TD([[subQ2,1.0]])],"derivedFrom":subQ1}),-1.0]])]});}
            var Q2;
            {var subQ0=sQuery(id+"F25.wireOp",EDGE,"E90");Q2=makeQuery(id+"F25.imprint","IMPRINT",FACE,{"disambiguationData":[TD([[makeQuery(id+"F25.imprint","IMPRINT",EDGE,{"derivedFrom":subQ0}),-1.0]])]});}
            var Q3;
            {var subQ0=sQuery(id+"F25.wireOp",EDGE,"E88");Q3=makeQuery(id+"F25.imprint","IMPRINT",FACE,{"disambiguationData":[TD([[makeQuery(id+"F25.imprint","IMPRINT",EDGE,{"derivedFrom":subQ0}),-1.0]])]});}
            var Q4;
            Q4=makeQuery(id+"F24.opPattern","COPY",FACE,{"derivedFrom":makeQuery(id+"F23.opLoft","SWEPT_FACE",FACE,{"disambiguationData":[OSD([sQuery(id+"F18.wireOp",EDGE,"E67"),sQuery(id+"F18.wireOp",EDGE,"E68"),sQuery(id+"F18.wireOp",EDGE,"E69"),sQuery(id+"F22.wireOp",EDGE,"E70"),sQuery(id+"F22.wireOp",EDGE,"E71"),sQuery(id+"F22.wireOp",EDGE,"E72")])]}),"instanceName":"1"});
            extrude(context, id + "F29", {"entities" : qUnion([Q0, Q1, Q2, Q3]), "endBound" : BoundingType.UP_TO_SURFACE, "depth" : 25.4 * mm, "endBoundEntityFace" : qUnion([Q4]), "offsetDistance" : 25.4 * mm});
        }
        {
            var Q0;
            {var subQ0=sQuery(id+"F0.wireOp",EDGE,"E16");Q0=makeQuery(id+"F0.imprint","IMPRINT",FACE,{"disambiguationData":[TD([[makeQuery(id+"F0.imprint","IMPRINT",EDGE,{"derivedFrom":subQ0}),1.0]])]});}
            extrude(context, id + "F30", {"entities" : qUnion([Q0]), "operationType" : NewBodyOperationType.ADD, "endBound" : BoundingType.SYMMETRIC, "depth" : 914.4 * mm, "offsetDistance" : 25.4 * mm});
        }
        {
            var Q0;
            Q0=makeQuery(id+"F23.opLoft","SWEPT_FACE",FACE,{"disambiguationData":[OSD([sQuery(id+"F18.wireOp",EDGE,"E67"),sQuery(id+"F18.wireOp",EDGE,"E68"),sQuery(id+"F18.wireOp",EDGE,"E69"),sQuery(id+"F22.wireOp",EDGE,"E70"),sQuery(id+"F22.wireOp",EDGE,"E71"),sQuery(id+"F22.wireOp",EDGE,"E72")])]});
            var sketch = newSketch(context, id + "F31", { "sketchPlane" : qUnion([Q0])});
            skLineSegment(sketch, "E91", {"start": v(21.27, 3346.46) * mm, "end": v(18.89, 3289.36) * mm});
            skLineSegment(sketch, "E92", {"start": v(18.89, 3289.36) * mm, "end": v(25.23, 3289.1) * mm});
            skLineSegment(sketch, "E93", {"start": v(25.23, 3289.1) * mm, "end": v(27.35, 3339.85) * mm});
            skLineSegment(sketch, "E94", {"start": v(33.96, 3345.93) * mm, "end": v(84.71, 3343.81) * mm});
            skLineSegment(sketch, "E95", {"start": v(84.71, 3343.81) * mm, "end": v(84.98, 3350.16) * mm});
            skLineSegment(sketch, "E96", {"start": v(84.98, 3350.16) * mm, "end": v(27.88, 3352.54) * mm});
            skLineSegment(sketch, "E97", {"start": v(-22.3, 24.23) * mm, "end": v(-24.94, -39.21) * mm});
            skLineSegment(sketch, "E98", {"start": v(-24.94, -39.21) * mm, "end": v(-18.6, -39.48) * mm});
            skLineSegment(sketch, "E99", {"start": v(-18.6, -39.48) * mm, "end": v(-16.21, 17.62) * mm});
            skLineSegment(sketch, "E100", {"start": v(-16.21, 17.62) * mm, "end": v(40.89, 15.24) * mm});
            skLineSegment(sketch, "E101", {"start": v(40.89, 15.24) * mm, "end": v(41.15, 21.59) * mm});
            skLineSegment(sketch, "E102", {"start": v(41.15, 21.59) * mm, "end": v(-22.3, 24.23) * mm});
            skPoint(sketch, "E103.visualSharp", {"position": v(27.61, 3346.2) * mm});
            skArc(sketch, "E103.filletArc", {"start": v(33.96, 3345.93) * mm, "mid": v(29.4, 3344.26) * mm, "end": v(27.35, 3339.85) * mm});
            skPoint(sketch, "E104.visualSharp", {"position": v(21.53, 3352.8) * mm});
            skArc(sketch, "E104.filletArc", {"start": v(27.88, 3352.54) * mm, "mid": v(23.31, 3350.86) * mm, "end": v(21.27, 3346.46) * mm});
            skSolve(sketch);
        }
        {
            var Q0;
            Q0=makeQuery(id+"F31.imprint","IMPRINT",FACE,{"disambiguationData":[TD([[makeQuery(id+"F31.imprint","IMPRINT",EDGE,{"derivedFrom":sQuery(id+"F31.wireOp",EDGE,"E91")}),-1.0]])]});
            var sketch = newSketch(context, id + "F32", { "sketchPlane" : qUnion([Q0])});
            skLineSegment(sketch, "E105", {"start": v(19.17, 2990.86) * mm, "end": v(15.62, 2933.82) * mm});
            skLineSegment(sketch, "E106", {"start": v(15.62, 2933.82) * mm, "end": v(21.96, 2933.43) * mm});
            skLineSegment(sketch, "E107", {"start": v(21.96, 2933.43) * mm, "end": v(25.11, 2984.13) * mm});
            skLineSegment(sketch, "E108", {"start": v(31.84, 2990.07) * mm, "end": v(69.87, 2987.71) * mm});
            skLineSegment(sketch, "E109", {"start": v(69.87, 2987.71) * mm, "end": v(70.26, 2994.05) * mm});
            skLineSegment(sketch, "E110", {"start": v(70.26, 2994.05) * mm, "end": v(25.9, 2996.8) * mm});
            skPoint(sketch, "E111.visualSharp", {"position": v(25.5, 2990.47) * mm});
            skArc(sketch, "E111.filletArc", {"start": v(31.84, 2990.07) * mm, "mid": v(27.25, 2988.5) * mm, "end": v(25.11, 2984.13) * mm});
            skPoint(sketch, "E112.visualSharp", {"position": v(19.56, 2997.2) * mm});
            skArc(sketch, "E112.filletArc", {"start": v(25.9, 2996.8) * mm, "mid": v(21.3, 2995.23) * mm, "end": v(19.17, 2990.86) * mm});
            skSolve(sketch);
        }
        {
            var Q0;
            Q0=makeQuery(id+"F31.imprint","IMPRINT",FACE,{"disambiguationData":[TD([[makeQuery(id+"F31.imprint","IMPRINT",EDGE,{"derivedFrom":sQuery(id+"F31.wireOp",EDGE,"E91")}),1.0]])]});
            var Q1;
            {var subQ1=sQuery(id+"F32.wireOp",EDGE,"E107");Q1=makeQuery(id+"F32.imprint","IMPRINT",FACE,{"disambiguationData":[TD([[makeQuery(id+"F32.imprint","IMPRINT",EDGE,{"derivedFrom":subQ1}),1.0]])]});}
            var Q2;
            {var subQ0=sQuery(id+"F32.wireOp",EDGE,"E105");Q2=makeQuery(id+"F32.imprint","IMPRINT",FACE,{"disambiguationData":[TD([[makeQuery(id+"F32.imprint","IMPRINT",EDGE,{"derivedFrom":subQ0}),1.0]])]});}
            var Q3;
            Q3=makeQuery(id+"F24.opPattern","COPY",FACE,{"derivedFrom":makeQuery(id+"F23.opLoft","SWEPT_FACE",FACE,{"disambiguationData":[OSD([sQuery(id+"F18.wireOp",EDGE,"E67"),sQuery(id+"F18.wireOp",EDGE,"E68"),sQuery(id+"F18.wireOp",EDGE,"E69"),sQuery(id+"F22.wireOp",EDGE,"E70"),sQuery(id+"F22.wireOp",EDGE,"E71"),sQuery(id+"F22.wireOp",EDGE,"E72")])]}),"instanceName":"1"});
            extrude(context, id + "F33", {"entities" : qUnion([Q0, Q1, Q2]), "endBound" : BoundingType.UP_TO_SURFACE, "depth" : 25.4 * mm, "endBoundEntityFace" : qUnion([Q3]), "offsetDistance" : 25.4 * mm});
        }
        {
            var Q0;
            {var subQ7=sQuery(id+"F2.wireOp",EDGE,"E24");var subQ10=sQuery(id+"F0.wireOp",EDGE,"E11.filletArc");var subQ13=sQuery(id+"F0.wireOp",EDGE,"E5");var subQ14=makeQuery(id+"F1.opExtrude","SWEPT_FACE",FACE,{"disambiguationData":[OSD([subQ13])]});var subQ15=makeQuery(id+"F3.opExtrude","SWEPT_FACE",FACE,{"disambiguationData":[OSD([subQ7])]});Q0=makeQuery(id+"F30.boolean.opBoolean","MERGE",FACE,{"derivedFrom":[makeQuery(id+"F4.boolean.opBoolean","SPLIT",FACE,{"disambiguationData":[TD([subQ15])],"derivedFrom":subQ14}),makeQuery(id+"F4.boolean.opBoolean","SPLIT",FACE,{"disambiguationData":[TD([makeQuery(id+"F4.opPattern","COPY",FACE,{"derivedFrom":subQ15,"instanceName":"1"})])],"derivedFrom":subQ14}),makeQuery(id+"F4.boolean.opBoolean","SPLIT",FACE,{"disambiguationData":[TD([makeQuery(id+"F1.opExtrude","SWEPT_FACE",FACE,{"disambiguationData":[OSD([subQ10])]})])],"derivedFrom":subQ14}),makeQuery(id+"F30.opExtrude","SWEPT_FACE",FACE,{"disambiguationData":[OSD([sQuery(id+"F0.wireOp",EDGE,"E19")])]})]});}
            var sketch = newSketch(context, id + "F34", { "sketchPlane" : qUnion([Q0])});
            skLineSegment(sketch, "E113", {"start": v(228.6, -457.2) * mm, "end": v(228.6, -342.9) * mm});
            skLineSegment(sketch, "E114", {"start": v(222.25, -336.55) * mm, "end": v(118.95, -336.55) * mm});
            skLineSegment(sketch, "E115", {"start": v(112.6, -342.9) * mm, "end": v(112.6, -406.4) * mm});
            skLineSegment(sketch, "E116", {"start": v(112.6, -406.4) * mm, "end": v(106.25, -406.4) * mm});
            skLineSegment(sketch, "E117", {"start": v(106.25, -406.4) * mm, "end": v(106.25, -336.55) * mm});
            skLineSegment(sketch, "E118", {"start": v(112.6, -330.2) * mm, "end": v(228.6, -330.2) * mm});
            skLineSegment(sketch, "E119", {"start": v(234.95, -336.55) * mm, "end": v(234.95, -457.2) * mm});
            skLineSegment(sketch, "E120", {"start": v(234.95, -457.2) * mm, "end": v(228.6, -457.2) * mm});
            skPoint(sketch, "E121.visualSharp", {"position": v(228.6, -336.55) * mm});
            skArc(sketch, "E121.filletArc", {"start": v(228.6, -342.9) * mm, "mid": v(226.74, -338.4) * mm, "end": v(222.25, -336.55) * mm});
            skPoint(sketch, "E122.visualSharp", {"position": v(112.6, -336.55) * mm});
            skArc(sketch, "E122.filletArc", {"start": v(118.95, -336.55) * mm, "mid": v(114.46, -338.4) * mm, "end": v(112.6, -342.9) * mm});
            skPoint(sketch, "E123.visualSharp", {"position": v(106.25, -330.2) * mm});
            skArc(sketch, "E123.filletArc", {"start": v(112.6, -330.2) * mm, "mid": v(108.1, -332.06) * mm, "end": v(106.25, -336.55) * mm});
            skPoint(sketch, "E124.visualSharp", {"position": v(234.95, -330.2) * mm});
            skArc(sketch, "E124.filletArc", {"start": v(234.95, -336.55) * mm, "mid": v(233.1, -332.06) * mm, "end": v(228.6, -330.2) * mm});
            skSolve(sketch);
        }
        {
            var Q0;
            Q0=makeQuery(id+"F34.imprint","IMPRINT",FACE,{"disambiguationData":[TD([[makeQuery(id+"F34.imprint","IMPRINT",EDGE,{"derivedFrom":sQuery(id+"F34.wireOp",EDGE,"E113")}),-1.0]])]});
            var Q1;
            Q1=makeQuery(id+"F8.opExtrude","SWEPT_FACE",FACE,{"disambiguationData":[OSD([sQuery(id+"F7.wireOp",EDGE,"E44")])]});
            extrude(context, id + "F35", {"entities" : qUnion([Q0]), "depth" : 863.6 * mm, "endBoundEntityFace" : qUnion([Q1]), "offsetDistance" : 25.4 * mm});
        }
        {
            var Q0;
            Q0=makeQuery(id+"F35.opExtrude","SWEPT_BODY",BODY,{"disambiguationData":[OSD([sQuery(id+"F34.wireOp",EDGE,"E113"),sQuery(id+"F34.wireOp",EDGE,"E114"),sQuery(id+"F34.wireOp",EDGE,"E115"),sQuery(id+"F34.wireOp",EDGE,"E116"),sQuery(id+"F34.wireOp",EDGE,"E117"),sQuery(id+"F34.wireOp",EDGE,"E118"),sQuery(id+"F34.wireOp",EDGE,"E119"),sQuery(id+"F34.wireOp",EDGE,"E120"),sQuery(id+"F34.wireOp",EDGE,"E121.filletArc"),sQuery(id+"F34.wireOp",EDGE,"E122.filletArc"),sQuery(id+"F34.wireOp",EDGE,"E123.filletArc"),sQuery(id+"F34.wireOp",EDGE,"E124.filletArc")])]});
            var Q1;
            Q1=qCreatedBy(makeId("Front.planeOp"),FACE);
            mirror(context, id + "F36", {"entities" : qUnion([Q0]), "mirrorPlane" : qUnion([Q1])});
        }
        {
            var Q0;
            Q0=makeQuery(id+"F11.opPattern","COPY",FACE,{"derivedFrom":makeQuery(id+"F10.opExtrude","SWEPT_FACE",FACE,{"disambiguationData":[OSD([sQuery(id+"F7.wireOp",EDGE,"E40")])]}),"instanceName":"1"});
            var sketch = newSketch(context, id + "F37", { "sketchPlane" : qUnion([Q0])});
            skLineSegment(sketch, "E125", {"start": v(-330.2, 790.72) * mm, "end": v(-336.55, 787.72) * mm});
            skLineSegment(sketch, "E126", {"start": v(-336.55, 787.72) * mm, "end": v(-336.55, 2.74) * mm});
            skLineSegment(sketch, "E127", {"start": v(-336.55, 2.74) * mm, "end": v(-330.2, 2.74) * mm});
            skSolve(sketch);
        }
        {
            var Q0;
            Q0=makeQuery(id+"F37.imprint","IMPRINT",FACE,{"disambiguationData":[TD([[makeQuery(id+"F37.imprint","IMPRINT",EDGE,{"derivedFrom":sQuery(id+"F37.wireOp",EDGE,"E125")}),1.0]])]});
            var Q1;
            Q1=makeQuery(id+"F35.opExtrude","SWEPT_FACE",FACE,{"disambiguationData":[OSD([sQuery(id+"F34.wireOp",EDGE,"E117")])]});
            extrude(context, id + "F38", {"entities" : qUnion([Q0]), "endBound" : BoundingType.UP_TO_SURFACE, "depth" : 25.4 * mm, "endBoundEntityFace" : qUnion([Q1]), "offsetDistance" : 25.4 * mm});
        }
        {
            var Q0;
            Q0=makeQuery(id+"F38.opExtrude","SWEPT_BODY",BODY,{"disambiguationData":[OSD([sQuery(id+"F7.wireOp",EDGE,"E40"),sQuery(id+"F37.wireOp",EDGE,"E125"),sQuery(id+"F37.wireOp",EDGE,"E126"),sQuery(id+"F37.wireOp",EDGE,"E127")])]});
            var Q1;
            Q1=qCreatedBy(makeId("Front.planeOp"),FACE);
            mirror(context, id + "F39", {"entities" : qUnion([Q0]), "mirrorPlane" : qUnion([Q1])});
        }
        {
            var Q0;
            Q0=makeQuery(id+"F36.opPattern","COPY",FACE,{"derivedFrom":makeQuery(id+"F35.opExtrude","SWEPT_FACE",FACE,{"disambiguationData":[OSD([sQuery(id+"F34.wireOp",EDGE,"E120")])]}),"instanceName":"1"});
            var sketch = newSketch(context, id + "F40", { "sketchPlane" : qUnion([Q0])});
            skLineSegment(sketch, "E128", {"start": v(-234.95, 869.95) * mm, "end": v(-234.95, 990.6) * mm});
            skLineSegment(sketch, "E129", {"start": v(-234.95, 990.6) * mm, "end": v(-228.6, 990.6) * mm});
            skLineSegment(sketch, "E130", {"start": v(-228.6, 990.6) * mm, "end": v(-228.6, 876.3) * mm});
            skLineSegment(sketch, "E131", {"start": v(-222.25, 869.95) * mm, "end": v(-112.6, 869.95) * mm});
            skLineSegment(sketch, "E132", {"start": v(-228.6, 863.6) * mm, "end": v(-112.6, 863.6) * mm});
            skLineSegment(sketch, "E133", {"start": v(-112.6, 863.6) * mm, "end": v(-112.6, 869.95) * mm});
            skPoint(sketch, "E134.visualSharp", {"position": v(-228.6, 869.95) * mm});
            skArc(sketch, "E134.filletArc", {"start": v(-228.6, 876.3) * mm, "mid": v(-226.74, 871.8) * mm, "end": v(-222.25, 869.95) * mm});
            skPoint(sketch, "E135.visualSharp", {"position": v(-234.95, 863.6) * mm});
            skArc(sketch, "E135.filletArc", {"start": v(-234.95, 869.95) * mm, "mid": v(-233.1, 865.46) * mm, "end": v(-228.6, 863.6) * mm});
            skSolve(sketch);
        }
        {
            var Q0;
            Q0=makeQuery(id+"F40.imprint","IMPRINT",FACE,{"disambiguationData":[TD([[makeQuery(id+"F40.imprint","IMPRINT",EDGE,{"derivedFrom":sQuery(id+"F40.wireOp",EDGE,"E128")}),-1.0]])]});
            var Q1;
            Q1=makeQuery(id+"F35.opExtrude","SWEPT_FACE",FACE,{"disambiguationData":[OSD([sQuery(id+"F34.wireOp",EDGE,"E120")])]});
            extrude(context, id + "F41", {"entities" : qUnion([Q0]), "endBound" : BoundingType.UP_TO_SURFACE, "oppositeDirection" : true, "depth" : 25.4 * mm, "endBoundEntityFace" : qUnion([Q1]), "offsetDistance" : 25.4 * mm});
        }
        {
            var Q0;
            Q0=makeQuery(id+"F8.opExtrude","SWEPT_FACE",FACE,{"disambiguationData":[OSD([sQuery(id+"F7.wireOp",EDGE,"E43")])]});
            var sketch = newSketch(context, id + "F42", { "sketchPlane" : qUnion([Q0])});
            skLineSegment(sketch, "E136", {"start": v(152.4, 996.95) * mm, "end": v(152.4, 869.95) * mm});
            skLineSegment(sketch, "E137", {"start": v(152.4, 869.95) * mm, "end": v(158.75, 869.95) * mm});
            skLineSegment(sketch, "E138", {"start": v(158.75, 869.95) * mm, "end": v(158.75, 996.95) * mm});
            skLineSegment(sketch, "E139", {"start": v(158.75, 996.95) * mm, "end": v(152.4, 996.95) * mm});
            skSolve(sketch);
        }
        {
            var Q0;
            {var subQ0=sQuery(id+"F42.wireOp",EDGE,"E139");Q0=makeQuery(id+"F42.imprint","IMPRINT",FACE,{"disambiguationData":[TD([[makeQuery(id+"F42.imprint","IMPRINT",EDGE,{"derivedFrom":subQ0}),1.0]])]});}
            var Q1;
            {var subQ0=sQuery(id+"F42.wireOp",EDGE,"E137");Q1=makeQuery(id+"F42.imprint","IMPRINT",FACE,{"disambiguationData":[TD([[makeQuery(id+"F42.imprint","IMPRINT",EDGE,{"derivedFrom":subQ0}),1.0]])]});}
            var Q2;
            Q2=makeQuery(id+"F41.opExtrude","SWEPT_FACE",FACE,{"disambiguationData":[OSD([sQuery(id+"F40.wireOp",EDGE,"E130")])]});
            extrude(context, id + "F43", {"entities" : qUnion([Q0, Q1]), "endBound" : BoundingType.UP_TO_SURFACE, "depth" : 25.4 * mm, "endBoundEntityFace" : qUnion([Q2]), "offsetDistance" : 25.4 * mm});
        }
        {
            var Q0;
            Q0=makeQuery(id+"F43.opExtrude","SWEPT_BODY",BODY,{"disambiguationData":[OSD([sQuery(id+"F42.wireOp",EDGE,"E136"),sQuery(id+"F42.wireOp",EDGE,"E137"),sQuery(id+"F42.wireOp",EDGE,"E138"),sQuery(id+"F42.wireOp",EDGE,"E139")])]});
            var Q1;
            Q1=qCreatedBy(makeId("Front.planeOp"),FACE);
            mirror(context, id + "F44", {"entities" : qUnion([Q0]), "mirrorPlane" : qUnion([Q1])});
        }
        {
            var Q0;
            Q0=qCreatedBy(makeId("Front.planeOp"),FACE);
            var sketch = newSketch(context, id + "F45", { "sketchPlane" : qUnion([Q0])});
            skLineSegment(sketch, "E140", {"start": v(234.95, -127) * mm, "end": v(6.35, -50.8) * mm});
            skLineSegment(sketch, "E141", {"start": v(234.95, -127) * mm, "end": v(234.95, -6.35) * mm});
            skLineSegment(sketch, "E142", {"start": v(234.95, -6.35) * mm, "end": v(6.35, -6.35) * mm});
            skLineSegment(sketch, "E143", {"start": v(6.35, -6.35) * mm, "end": v(6.35, -50.8) * mm});
            skSolve(sketch);
        }
        {
            var Q0;
            Q0=makeQuery(id+"F45.imprint","IMPRINT",FACE,{"disambiguationData":[TD([[makeQuery(id+"F45.imprint","IMPRINT",EDGE,{"derivedFrom":sQuery(id+"F45.wireOp",EDGE,"E140")}),-1.0]])]});
            extrude(context, id + "F46", {"entities" : qUnion([Q0]), "endBound" : BoundingType.SYMMETRIC, "depth" : 3.17 * mm, "offsetDistance" : 25.4 * mm});
        }
    });
